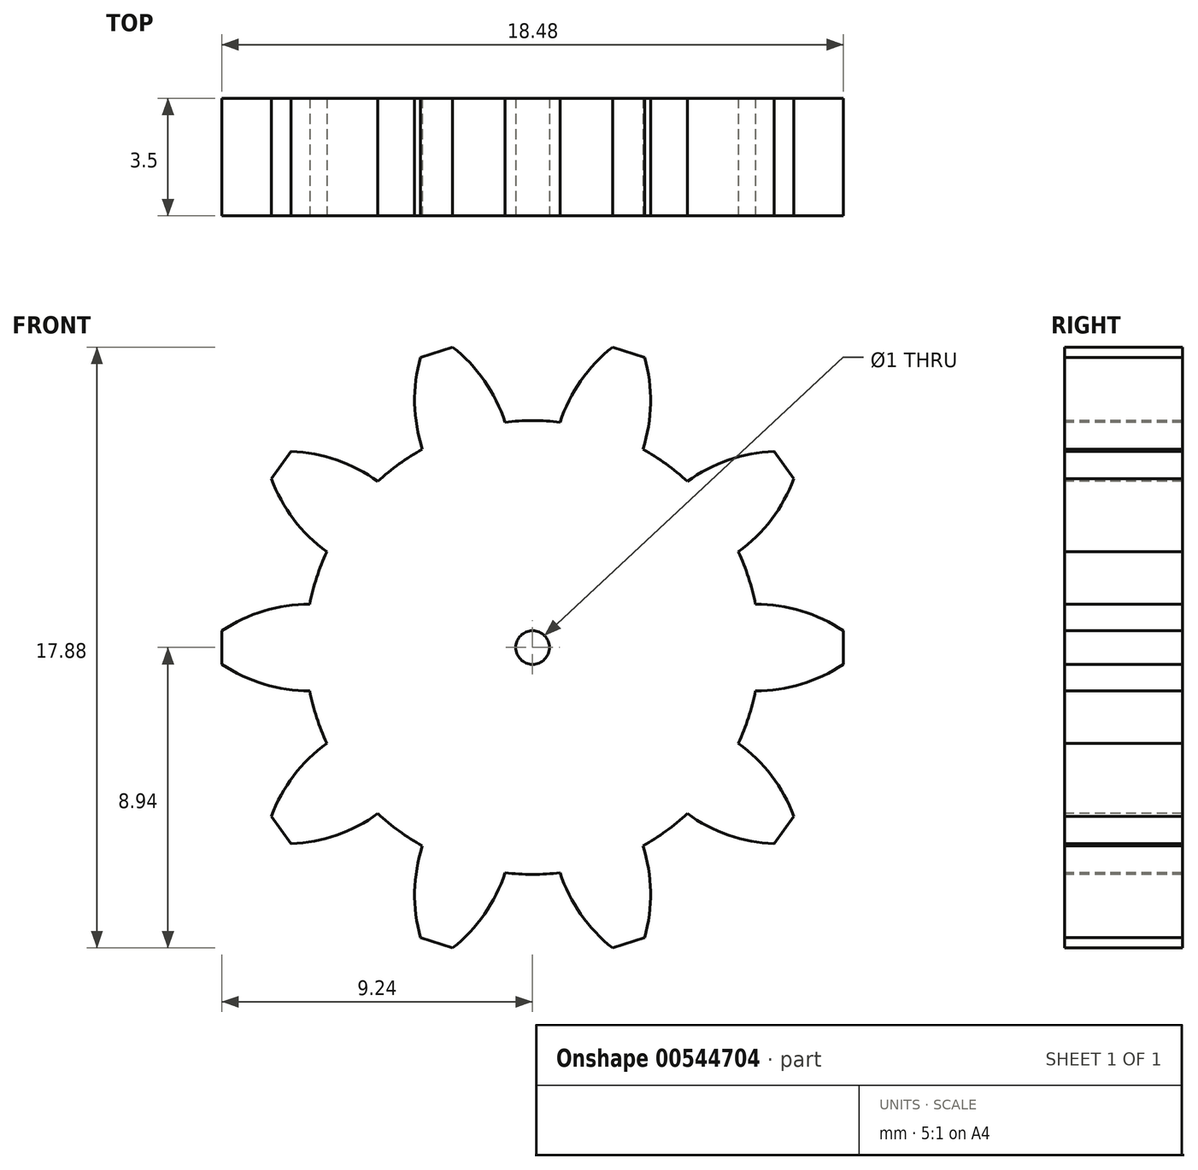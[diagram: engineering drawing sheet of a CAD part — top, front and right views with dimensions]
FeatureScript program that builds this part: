
annotation { "Feature Type Name" : "Feature", "Feature Type Description" : "" }
export const myFeature = defineFeature(function(context is Context, id is Id, definition is map)
    precondition{}
    {
        {
            var Q0;
            Q0=qCreatedBy(makeId("Front.planeOp"),FACE);
            var sketch = newSketch(context, id + "F0", { "sketchPlane" : qUnion([Q0])});
            skCircle(sketch, "E0", {"center": v(0, 0) * mm, "radius": 20 * mm, "construction": true});
            skCircle(sketch, "E1", {"center": v(0, 0) * mm, "radius": 24 * mm, "construction": true});
            skCircle(sketch, "E2", {"center": v(0, 0) * mm, "radius": 22.5 * mm, "construction": true});
            skPoint(sketch, "E3", {"position": v(0, 20) * mm});
            skPoint(sketch, "E4", {"position": v(-0.5, 20) * mm});
            skPoint(sketch, "E5", {"position": v(0.5, 20) * mm});
            skPoint(sketch, "E6", {"position": v(0, 22.5) * mm});
            skPoint(sketch, "E7", {"position": v(-1.3, 22.46) * mm});
            skPoint(sketch, "E8", {"position": v(1.3, 22.46) * mm});
            skArc(sketch, "E9", {"start": v(-1.3, 22.46) * mm, "mid": v(-1.1, 21.17) * mm, "end": v(-0.5, 20) * mm, "construction": true});
            skArc(sketch, "E10", {"start": v(0.5, 20) * mm, "mid": v(1.1, 21.17) * mm, "end": v(1.3, 22.46) * mm, "construction": true});
            skLineSegment(sketch, "E11", {"start": v(-0.5, 20) * mm, "end": v(0.5, 20) * mm, "construction": true});
            skPoint(sketch, "E12.1.0", {"position": v(-5.27, 19.3) * mm});
            skArc(sketch, "E12.1.1", {"start": v(-4.3, 19.53) * mm, "mid": v(-4, 20.81) * mm, "end": v(-4.11, 22.12) * mm, "construction": true});
            skArc(sketch, "E12.1.2", {"start": v(-6.64, 21.5) * mm, "mid": v(-6.13, 20.29) * mm, "end": v(-5.27, 19.3) * mm, "construction": true});
            skPoint(sketch, "E12.1.3", {"position": v(-6.64, 21.5) * mm});
            skPoint(sketch, "E12.1.4", {"position": v(-5.38, 21.85) * mm});
            skPoint(sketch, "E12.1.5", {"position": v(-4.3, 19.53) * mm});
            skPoint(sketch, "E12.1.6", {"position": v(-4.11, 22.12) * mm});
            skPoint(sketch, "E12.1.7", {"position": v(-4.79, 19.42) * mm});
            skLineSegment(sketch, "E12.1.8", {"start": v(-5.27, 19.3) * mm, "end": v(-4.3, 19.53) * mm, "construction": true});
            skPoint(sketch, "E12.2.0", {"position": v(-9.73, 17.47) * mm});
            skArc(sketch, "E12.2.1", {"start": v(-8.85, 17.94) * mm, "mid": v(-8.87, 19.25) * mm, "end": v(-9.29, 20.5) * mm, "construction": true});
            skArc(sketch, "E12.2.2", {"start": v(-11.59, 19.29) * mm, "mid": v(-10.8, 18.23) * mm, "end": v(-9.73, 17.47) * mm, "construction": true});
            skPoint(sketch, "E12.2.3", {"position": v(-11.59, 19.29) * mm});
            skPoint(sketch, "E12.2.4", {"position": v(-10.46, 19.92) * mm});
            skPoint(sketch, "E12.2.5", {"position": v(-8.85, 17.94) * mm});
            skPoint(sketch, "E12.2.6", {"position": v(-9.29, 20.5) * mm});
            skPoint(sketch, "E12.2.7", {"position": v(-9.3, 17.7) * mm});
            skLineSegment(sketch, "E12.2.8", {"start": v(-9.73, 17.47) * mm, "end": v(-8.85, 17.94) * mm, "construction": true});
            skPoint(sketch, "E12.3.0", {"position": v(-13.63, 14.63) * mm});
            skArc(sketch, "E12.3.1", {"start": v(-12.88, 15.3) * mm, "mid": v(-13.22, 16.57) * mm, "end": v(-13.92, 17.67) * mm, "construction": true});
            skArc(sketch, "E12.3.2", {"start": v(-15.87, 15.95) * mm, "mid": v(-14.85, 15.12) * mm, "end": v(-13.63, 14.63) * mm, "construction": true});
            skPoint(sketch, "E12.3.3", {"position": v(-15.87, 15.95) * mm});
            skPoint(sketch, "E12.3.4", {"position": v(-14.92, 16.84) * mm});
            skPoint(sketch, "E12.3.5", {"position": v(-12.88, 15.3) * mm});
            skPoint(sketch, "E12.3.6", {"position": v(-13.92, 17.67) * mm});
            skPoint(sketch, "E12.3.7", {"position": v(-13.26, 14.97) * mm});
            skLineSegment(sketch, "E12.3.8", {"start": v(-13.63, 14.63) * mm, "end": v(-12.88, 15.3) * mm, "construction": true});
            skPoint(sketch, "E12.4.0", {"position": v(-16.74, 10.95) * mm});
            skArc(sketch, "E12.4.1", {"start": v(-16.17, 11.77) * mm, "mid": v(-16.8, 12.92) * mm, "end": v(-17.75, 13.83) * mm, "construction": true});
            skArc(sketch, "E12.4.2", {"start": v(-19.22, 11.7) * mm, "mid": v(-18.04, 11.12) * mm, "end": v(-16.74, 10.95) * mm, "construction": true});
            skPoint(sketch, "E12.4.3", {"position": v(-19.22, 11.7) * mm});
            skPoint(sketch, "E12.4.4", {"position": v(-18.52, 12.78) * mm});
            skPoint(sketch, "E12.4.5", {"position": v(-16.17, 11.77) * mm});
            skPoint(sketch, "E12.4.6", {"position": v(-17.75, 13.83) * mm});
            skPoint(sketch, "E12.4.7", {"position": v(-16.46, 11.36) * mm});
            skLineSegment(sketch, "E12.4.8", {"start": v(-16.74, 10.95) * mm, "end": v(-16.17, 11.77) * mm, "construction": true});
            skPoint(sketch, "E12.5.0", {"position": v(-18.87, 6.62) * mm});
            skArc(sketch, "E12.5.1", {"start": v(-18.52, 7.56) * mm, "mid": v(-19.4, 8.53) * mm, "end": v(-20.54, 9.18) * mm, "construction": true});
            skArc(sketch, "E12.5.2", {"start": v(-21.46, 6.75) * mm, "mid": v(-20.18, 6.48) * mm, "end": v(-18.87, 6.62) * mm, "construction": true});
            skPoint(sketch, "E12.5.3", {"position": v(-21.46, 6.75) * mm});
            skPoint(sketch, "E12.5.4", {"position": v(-21.04, 7.98) * mm});
            skPoint(sketch, "E12.5.5", {"position": v(-18.52, 7.56) * mm});
            skPoint(sketch, "E12.5.6", {"position": v(-20.54, 9.18) * mm});
            skPoint(sketch, "E12.5.7", {"position": v(-18.7, 7.1) * mm});
            skLineSegment(sketch, "E12.5.8", {"start": v(-18.87, 6.62) * mm, "end": v(-18.52, 7.56) * mm, "construction": true});
            skPoint(sketch, "E12.6.0", {"position": v(-19.9, 1.91) * mm});
            skArc(sketch, "E12.6.1", {"start": v(-19.79, 2.9) * mm, "mid": v(-20.88, 3.64) * mm, "end": v(-22.14, 4) * mm, "construction": true});
            skArc(sketch, "E12.6.2", {"start": v(-22.46, 1.42) * mm, "mid": v(-21.14, 1.46) * mm, "end": v(-19.9, 1.91) * mm, "construction": true});
            skPoint(sketch, "E12.6.3", {"position": v(-22.46, 1.42) * mm});
            skPoint(sketch, "E12.6.4", {"position": v(-22.34, 2.71) * mm});
            skPoint(sketch, "E12.6.5", {"position": v(-19.79, 2.9) * mm});
            skPoint(sketch, "E12.6.6", {"position": v(-22.14, 4) * mm});
            skPoint(sketch, "E12.6.7", {"position": v(-19.85, 2.41) * mm});
            skLineSegment(sketch, "E12.6.8", {"start": v(-19.9, 1.91) * mm, "end": v(-19.79, 2.9) * mm, "construction": true});
            skPoint(sketch, "E12.7.0", {"position": v(-19.79, -2.9) * mm});
            skArc(sketch, "E12.7.1", {"start": v(-19.9, -1.91) * mm, "mid": v(-21.14, -1.46) * mm, "end": v(-22.46, -1.42) * mm, "construction": true});
            skArc(sketch, "E12.7.2", {"start": v(-22.14, -4) * mm, "mid": v(-20.88, -3.64) * mm, "end": v(-19.79, -2.9) * mm, "construction": true});
            skPoint(sketch, "E12.7.3", {"position": v(-22.14, -4) * mm});
            skPoint(sketch, "E12.7.4", {"position": v(-22.34, -2.71) * mm});
            skPoint(sketch, "E12.7.5", {"position": v(-19.9, -1.91) * mm});
            skPoint(sketch, "E12.7.6", {"position": v(-22.46, -1.42) * mm});
            skPoint(sketch, "E12.7.7", {"position": v(-19.85, -2.41) * mm});
            skLineSegment(sketch, "E12.7.8", {"start": v(-19.79, -2.9) * mm, "end": v(-19.9, -1.91) * mm, "construction": true});
            skPoint(sketch, "E12.8.0", {"position": v(-18.52, -7.56) * mm});
            skArc(sketch, "E12.8.1", {"start": v(-18.87, -6.62) * mm, "mid": v(-20.18, -6.48) * mm, "end": v(-21.46, -6.75) * mm, "construction": true});
            skArc(sketch, "E12.8.2", {"start": v(-20.54, -9.18) * mm, "mid": v(-19.4, -8.53) * mm, "end": v(-18.52, -7.56) * mm, "construction": true});
            skPoint(sketch, "E12.8.3", {"position": v(-20.54, -9.18) * mm});
            skPoint(sketch, "E12.8.4", {"position": v(-21.04, -7.98) * mm});
            skPoint(sketch, "E12.8.5", {"position": v(-18.87, -6.62) * mm});
            skPoint(sketch, "E12.8.6", {"position": v(-21.46, -6.75) * mm});
            skPoint(sketch, "E12.8.7", {"position": v(-18.7, -7.1) * mm});
            skLineSegment(sketch, "E12.8.8", {"start": v(-18.52, -7.56) * mm, "end": v(-18.87, -6.62) * mm, "construction": true});
            skPoint(sketch, "E12.9.0", {"position": v(-16.17, -11.77) * mm});
            skArc(sketch, "E12.9.1", {"start": v(-16.74, -10.95) * mm, "mid": v(-18.04, -11.12) * mm, "end": v(-19.22, -11.7) * mm, "construction": true});
            skArc(sketch, "E12.9.2", {"start": v(-17.75, -13.83) * mm, "mid": v(-16.8, -12.92) * mm, "end": v(-16.17, -11.77) * mm, "construction": true});
            skPoint(sketch, "E12.9.3", {"position": v(-17.75, -13.83) * mm});
            skPoint(sketch, "E12.9.4", {"position": v(-18.52, -12.78) * mm});
            skPoint(sketch, "E12.9.5", {"position": v(-16.74, -10.95) * mm});
            skPoint(sketch, "E12.9.6", {"position": v(-19.22, -11.7) * mm});
            skPoint(sketch, "E12.9.7", {"position": v(-16.46, -11.36) * mm});
            skLineSegment(sketch, "E12.9.8", {"start": v(-16.17, -11.77) * mm, "end": v(-16.74, -10.95) * mm, "construction": true});
            skPoint(sketch, "E12.10.0", {"position": v(-12.88, -15.3) * mm});
            skArc(sketch, "E12.10.1", {"start": v(-13.63, -14.63) * mm, "mid": v(-14.85, -15.12) * mm, "end": v(-15.87, -15.95) * mm, "construction": true});
            skArc(sketch, "E12.10.2", {"start": v(-13.92, -17.67) * mm, "mid": v(-13.22, -16.57) * mm, "end": v(-12.88, -15.3) * mm, "construction": true});
            skPoint(sketch, "E12.10.3", {"position": v(-13.92, -17.67) * mm});
            skPoint(sketch, "E12.10.4", {"position": v(-14.92, -16.84) * mm});
            skPoint(sketch, "E12.10.5", {"position": v(-13.63, -14.63) * mm});
            skPoint(sketch, "E12.10.6", {"position": v(-15.87, -15.95) * mm});
            skPoint(sketch, "E12.10.7", {"position": v(-13.26, -14.97) * mm});
            skLineSegment(sketch, "E12.10.8", {"start": v(-12.88, -15.3) * mm, "end": v(-13.63, -14.63) * mm, "construction": true});
            skPoint(sketch, "E12.11.0", {"position": v(-8.85, -17.94) * mm});
            skArc(sketch, "E12.11.1", {"start": v(-9.73, -17.47) * mm, "mid": v(-10.8, -18.23) * mm, "end": v(-11.59, -19.29) * mm, "construction": true});
            skArc(sketch, "E12.11.2", {"start": v(-9.29, -20.5) * mm, "mid": v(-8.87, -19.25) * mm, "end": v(-8.85, -17.94) * mm, "construction": true});
            skPoint(sketch, "E12.11.3", {"position": v(-9.29, -20.5) * mm});
            skPoint(sketch, "E12.11.4", {"position": v(-10.46, -19.92) * mm});
            skPoint(sketch, "E12.11.5", {"position": v(-9.73, -17.47) * mm});
            skPoint(sketch, "E12.11.6", {"position": v(-11.59, -19.29) * mm});
            skPoint(sketch, "E12.11.7", {"position": v(-9.3, -17.7) * mm});
            skLineSegment(sketch, "E12.11.8", {"start": v(-8.85, -17.94) * mm, "end": v(-9.73, -17.47) * mm, "construction": true});
            skPoint(sketch, "E12.12.0", {"position": v(-4.3, -19.53) * mm});
            skArc(sketch, "E12.12.1", {"start": v(-5.27, -19.3) * mm, "mid": v(-6.13, -20.29) * mm, "end": v(-6.64, -21.5) * mm, "construction": true});
            skArc(sketch, "E12.12.2", {"start": v(-4.11, -22.12) * mm, "mid": v(-4, -20.81) * mm, "end": v(-4.3, -19.53) * mm, "construction": true});
            skPoint(sketch, "E12.12.3", {"position": v(-4.11, -22.12) * mm});
            skPoint(sketch, "E12.12.4", {"position": v(-5.38, -21.85) * mm});
            skPoint(sketch, "E12.12.5", {"position": v(-5.27, -19.3) * mm});
            skPoint(sketch, "E12.12.6", {"position": v(-6.64, -21.5) * mm});
            skPoint(sketch, "E12.12.7", {"position": v(-4.79, -19.42) * mm});
            skLineSegment(sketch, "E12.12.8", {"start": v(-4.3, -19.53) * mm, "end": v(-5.27, -19.3) * mm, "construction": true});
            skPoint(sketch, "E12.13.0", {"position": v(0.5, -20) * mm});
            skArc(sketch, "E12.13.1", {"start": v(-0.5, -20) * mm, "mid": v(-1.1, -21.17) * mm, "end": v(-1.3, -22.46) * mm, "construction": true});
            skArc(sketch, "E12.13.2", {"start": v(1.3, -22.46) * mm, "mid": v(1.1, -21.17) * mm, "end": v(0.5, -20) * mm, "construction": true});
            skPoint(sketch, "E12.13.3", {"position": v(1.3, -22.46) * mm});
            skPoint(sketch, "E12.13.4", {"position": v(0, -22.5) * mm});
            skPoint(sketch, "E12.13.5", {"position": v(-0.5, -20) * mm});
            skPoint(sketch, "E12.13.6", {"position": v(-1.3, -22.46) * mm});
            skPoint(sketch, "E12.13.7", {"position": v(0, -20) * mm});
            skLineSegment(sketch, "E12.13.8", {"start": v(0.5, -20) * mm, "end": v(-0.5, -20) * mm, "construction": true});
            skPoint(sketch, "E12.14.0", {"position": v(5.27, -19.3) * mm});
            skArc(sketch, "E12.14.1", {"start": v(4.3, -19.53) * mm, "mid": v(4, -20.81) * mm, "end": v(4.11, -22.12) * mm, "construction": true});
            skArc(sketch, "E12.14.2", {"start": v(6.64, -21.5) * mm, "mid": v(6.13, -20.29) * mm, "end": v(5.27, -19.3) * mm, "construction": true});
            skPoint(sketch, "E12.14.3", {"position": v(6.64, -21.5) * mm});
            skPoint(sketch, "E12.14.4", {"position": v(5.38, -21.85) * mm});
            skPoint(sketch, "E12.14.5", {"position": v(4.3, -19.53) * mm});
            skPoint(sketch, "E12.14.6", {"position": v(4.11, -22.12) * mm});
            skPoint(sketch, "E12.14.7", {"position": v(4.79, -19.42) * mm});
            skLineSegment(sketch, "E12.14.8", {"start": v(5.27, -19.3) * mm, "end": v(4.3, -19.53) * mm, "construction": true});
            skPoint(sketch, "E12.15.0", {"position": v(9.73, -17.47) * mm});
            skArc(sketch, "E12.15.1", {"start": v(8.85, -17.94) * mm, "mid": v(8.87, -19.25) * mm, "end": v(9.29, -20.5) * mm, "construction": true});
            skArc(sketch, "E12.15.2", {"start": v(11.59, -19.29) * mm, "mid": v(10.8, -18.23) * mm, "end": v(9.73, -17.47) * mm, "construction": true});
            skPoint(sketch, "E12.15.3", {"position": v(11.59, -19.29) * mm});
            skPoint(sketch, "E12.15.4", {"position": v(10.46, -19.92) * mm});
            skPoint(sketch, "E12.15.5", {"position": v(8.85, -17.94) * mm});
            skPoint(sketch, "E12.15.6", {"position": v(9.29, -20.5) * mm});
            skPoint(sketch, "E12.15.7", {"position": v(9.3, -17.7) * mm});
            skLineSegment(sketch, "E12.15.8", {"start": v(9.73, -17.47) * mm, "end": v(8.85, -17.94) * mm, "construction": true});
            skPoint(sketch, "E12.16.0", {"position": v(13.63, -14.63) * mm});
            skArc(sketch, "E12.16.1", {"start": v(12.88, -15.3) * mm, "mid": v(13.22, -16.57) * mm, "end": v(13.92, -17.67) * mm, "construction": true});
            skArc(sketch, "E12.16.2", {"start": v(15.87, -15.95) * mm, "mid": v(14.85, -15.12) * mm, "end": v(13.63, -14.63) * mm, "construction": true});
            skPoint(sketch, "E12.16.3", {"position": v(15.87, -15.95) * mm});
            skPoint(sketch, "E12.16.4", {"position": v(14.92, -16.84) * mm});
            skPoint(sketch, "E12.16.5", {"position": v(12.88, -15.3) * mm});
            skPoint(sketch, "E12.16.6", {"position": v(13.92, -17.67) * mm});
            skPoint(sketch, "E12.16.7", {"position": v(13.26, -14.97) * mm});
            skLineSegment(sketch, "E12.16.8", {"start": v(13.63, -14.63) * mm, "end": v(12.88, -15.3) * mm, "construction": true});
            skPoint(sketch, "E12.17.0", {"position": v(16.74, -10.95) * mm});
            skArc(sketch, "E12.17.1", {"start": v(16.17, -11.77) * mm, "mid": v(16.8, -12.92) * mm, "end": v(17.75, -13.83) * mm, "construction": true});
            skArc(sketch, "E12.17.2", {"start": v(19.22, -11.7) * mm, "mid": v(18.04, -11.12) * mm, "end": v(16.74, -10.95) * mm, "construction": true});
            skPoint(sketch, "E12.17.3", {"position": v(19.22, -11.7) * mm});
            skPoint(sketch, "E12.17.4", {"position": v(18.52, -12.78) * mm});
            skPoint(sketch, "E12.17.5", {"position": v(16.17, -11.77) * mm});
            skPoint(sketch, "E12.17.6", {"position": v(17.75, -13.83) * mm});
            skPoint(sketch, "E12.17.7", {"position": v(16.46, -11.36) * mm});
            skLineSegment(sketch, "E12.17.8", {"start": v(16.74, -10.95) * mm, "end": v(16.17, -11.77) * mm, "construction": true});
            skPoint(sketch, "E12.18.0", {"position": v(18.87, -6.62) * mm});
            skArc(sketch, "E12.18.1", {"start": v(18.52, -7.56) * mm, "mid": v(19.4, -8.53) * mm, "end": v(20.54, -9.18) * mm, "construction": true});
            skArc(sketch, "E12.18.2", {"start": v(21.46, -6.75) * mm, "mid": v(20.18, -6.48) * mm, "end": v(18.87, -6.62) * mm, "construction": true});
            skPoint(sketch, "E12.18.3", {"position": v(21.46, -6.75) * mm});
            skPoint(sketch, "E12.18.4", {"position": v(21.04, -7.98) * mm});
            skPoint(sketch, "E12.18.5", {"position": v(18.52, -7.56) * mm});
            skPoint(sketch, "E12.18.6", {"position": v(20.54, -9.18) * mm});
            skPoint(sketch, "E12.18.7", {"position": v(18.7, -7.1) * mm});
            skLineSegment(sketch, "E12.18.8", {"start": v(18.87, -6.62) * mm, "end": v(18.52, -7.56) * mm, "construction": true});
            skPoint(sketch, "E12.19.0", {"position": v(19.9, -1.91) * mm});
            skArc(sketch, "E12.19.1", {"start": v(19.79, -2.9) * mm, "mid": v(20.88, -3.64) * mm, "end": v(22.14, -4) * mm, "construction": true});
            skArc(sketch, "E12.19.2", {"start": v(22.46, -1.42) * mm, "mid": v(21.14, -1.46) * mm, "end": v(19.9, -1.91) * mm, "construction": true});
            skPoint(sketch, "E12.19.3", {"position": v(22.46, -1.42) * mm});
            skPoint(sketch, "E12.19.4", {"position": v(22.34, -2.71) * mm});
            skPoint(sketch, "E12.19.5", {"position": v(19.79, -2.9) * mm});
            skPoint(sketch, "E12.19.6", {"position": v(22.14, -4) * mm});
            skPoint(sketch, "E12.19.7", {"position": v(19.85, -2.41) * mm});
            skLineSegment(sketch, "E12.19.8", {"start": v(19.9, -1.91) * mm, "end": v(19.79, -2.9) * mm, "construction": true});
            skPoint(sketch, "E12.20.0", {"position": v(19.79, 2.9) * mm});
            skArc(sketch, "E12.20.1", {"start": v(19.9, 1.91) * mm, "mid": v(21.14, 1.46) * mm, "end": v(22.46, 1.42) * mm, "construction": true});
            skArc(sketch, "E12.20.2", {"start": v(22.14, 4) * mm, "mid": v(20.88, 3.64) * mm, "end": v(19.79, 2.9) * mm, "construction": true});
            skPoint(sketch, "E12.20.3", {"position": v(22.14, 4) * mm});
            skPoint(sketch, "E12.20.4", {"position": v(22.34, 2.71) * mm});
            skPoint(sketch, "E12.20.5", {"position": v(19.9, 1.91) * mm});
            skPoint(sketch, "E12.20.6", {"position": v(22.46, 1.42) * mm});
            skPoint(sketch, "E12.20.7", {"position": v(19.85, 2.41) * mm});
            skLineSegment(sketch, "E12.20.8", {"start": v(19.79, 2.9) * mm, "end": v(19.9, 1.91) * mm, "construction": true});
            skPoint(sketch, "E12.21.0", {"position": v(18.52, 7.56) * mm});
            skArc(sketch, "E12.21.1", {"start": v(18.87, 6.62) * mm, "mid": v(20.18, 6.48) * mm, "end": v(21.46, 6.75) * mm, "construction": true});
            skArc(sketch, "E12.21.2", {"start": v(20.54, 9.18) * mm, "mid": v(19.4, 8.53) * mm, "end": v(18.52, 7.56) * mm, "construction": true});
            skPoint(sketch, "E12.21.3", {"position": v(20.54, 9.18) * mm});
            skPoint(sketch, "E12.21.4", {"position": v(21.04, 7.98) * mm});
            skPoint(sketch, "E12.21.5", {"position": v(18.87, 6.62) * mm});
            skPoint(sketch, "E12.21.6", {"position": v(21.46, 6.75) * mm});
            skPoint(sketch, "E12.21.7", {"position": v(18.7, 7.1) * mm});
            skLineSegment(sketch, "E12.21.8", {"start": v(18.52, 7.56) * mm, "end": v(18.87, 6.62) * mm, "construction": true});
            skPoint(sketch, "E12.22.0", {"position": v(16.17, 11.77) * mm});
            skArc(sketch, "E12.22.1", {"start": v(16.74, 10.95) * mm, "mid": v(18.04, 11.12) * mm, "end": v(19.22, 11.7) * mm, "construction": true});
            skArc(sketch, "E12.22.2", {"start": v(17.75, 13.83) * mm, "mid": v(16.8, 12.92) * mm, "end": v(16.17, 11.77) * mm, "construction": true});
            skPoint(sketch, "E12.22.3", {"position": v(17.75, 13.83) * mm});
            skPoint(sketch, "E12.22.4", {"position": v(18.52, 12.78) * mm});
            skPoint(sketch, "E12.22.5", {"position": v(16.74, 10.95) * mm});
            skPoint(sketch, "E12.22.6", {"position": v(19.22, 11.7) * mm});
            skPoint(sketch, "E12.22.7", {"position": v(16.46, 11.36) * mm});
            skLineSegment(sketch, "E12.22.8", {"start": v(16.17, 11.77) * mm, "end": v(16.74, 10.95) * mm, "construction": true});
            skPoint(sketch, "E12.23.0", {"position": v(12.88, 15.3) * mm});
            skArc(sketch, "E12.23.1", {"start": v(13.63, 14.63) * mm, "mid": v(14.85, 15.12) * mm, "end": v(15.87, 15.95) * mm, "construction": true});
            skArc(sketch, "E12.23.2", {"start": v(13.92, 17.67) * mm, "mid": v(13.22, 16.57) * mm, "end": v(12.88, 15.3) * mm, "construction": true});
            skPoint(sketch, "E12.23.3", {"position": v(13.92, 17.67) * mm});
            skPoint(sketch, "E12.23.4", {"position": v(14.92, 16.84) * mm});
            skPoint(sketch, "E12.23.5", {"position": v(13.63, 14.63) * mm});
            skPoint(sketch, "E12.23.6", {"position": v(15.87, 15.95) * mm});
            skPoint(sketch, "E12.23.7", {"position": v(13.26, 14.97) * mm});
            skLineSegment(sketch, "E12.23.8", {"start": v(12.88, 15.3) * mm, "end": v(13.63, 14.63) * mm, "construction": true});
            skPoint(sketch, "E12.24.0", {"position": v(8.85, 17.94) * mm});
            skArc(sketch, "E12.24.1", {"start": v(9.73, 17.47) * mm, "mid": v(10.8, 18.23) * mm, "end": v(11.59, 19.29) * mm, "construction": true});
            skArc(sketch, "E12.24.2", {"start": v(9.29, 20.5) * mm, "mid": v(8.87, 19.25) * mm, "end": v(8.85, 17.94) * mm, "construction": true});
            skPoint(sketch, "E12.24.3", {"position": v(9.29, 20.5) * mm});
            skPoint(sketch, "E12.24.4", {"position": v(10.46, 19.92) * mm});
            skPoint(sketch, "E12.24.5", {"position": v(9.73, 17.47) * mm});
            skPoint(sketch, "E12.24.6", {"position": v(11.59, 19.29) * mm});
            skPoint(sketch, "E12.24.7", {"position": v(9.3, 17.7) * mm});
            skLineSegment(sketch, "E12.24.8", {"start": v(8.85, 17.94) * mm, "end": v(9.73, 17.47) * mm, "construction": true});
            skPoint(sketch, "E13.0.25.0", {"position": v(4.3, 19.53) * mm});
            skArc(sketch, "E13.1.25.0", {"start": v(5.27, 19.3) * mm, "mid": v(6.13, 20.29) * mm, "end": v(6.64, 21.5) * mm, "construction": true});
            skArc(sketch, "E13.5.25.0", {"start": v(4.11, 22.12) * mm, "mid": v(4, 20.81) * mm, "end": v(4.3, 19.53) * mm, "construction": true});
            skPoint(sketch, "E13.9.25.0", {"position": v(4.11, 22.12) * mm});
            skPoint(sketch, "E13.10.25.0", {"position": v(5.38, 21.85) * mm});
            skPoint(sketch, "E13.11.25.0", {"position": v(5.27, 19.3) * mm});
            skPoint(sketch, "E13.12.25.0", {"position": v(6.64, 21.5) * mm});
            skPoint(sketch, "E13.13.25.0", {"position": v(4.79, 19.42) * mm});
            skLineSegment(sketch, "E13.14.25.0", {"start": v(4.3, 19.53) * mm, "end": v(5.27, 19.3) * mm, "construction": true});
            skArc(sketch, "E14", {"start": v(-22.46, -1.42) * mm, "mid": v(-22.5, 0) * mm, "end": v(-22.46, 1.42) * mm});
            skPoint(sketch, "E15", {"position": v(-22.5, 0) * mm});
            skLineSegment(sketch, "E16", {"start": v(-22.5, 0) * mm, "end": v(0, 0) * mm, "construction": true});
            skCircle(sketch, "E17", {"center": v(0, 0) * mm, "radius": 4 * mm, "construction": true});
            skCircle(sketch, "E18", {"center": v(0, 0) * mm, "radius": 1.5 * mm, "construction": true});
            skPoint(sketch, "E19", {"position": v(-20, 0) * mm});
            skLineSegment(sketch, "E20", {"start": v(-20, 0) * mm, "end": v(-22.5, 0) * mm});
            skLineSegment(sketch, "E21", {"start": v(-1.5, 0) * mm, "end": v(-4, 0) * mm});
            skPoint(sketch, "E22", {"position": v(-2.75, 0) * mm});
            skPoint(sketch, "E23", {"position": v(-21.25, 0) * mm});
            skCircle(sketch, "E24", {"center": v(-12, 0) * mm, "radius": 9.25 * mm, "construction": true});
            skCircle(sketch, "E25", {"center": v(-12, 0) * mm, "radius": 6.75 * mm});
            skPoint(sketch, "E26", {"position": v(-18.75, 0) * mm});
            skPoint(sketch, "E27", {"position": v(-18.63, 1.3) * mm});
            skPoint(sketch, "E28", {"position": v(-18.63, -1.3) * mm});
            skPoint(sketch, "E29", {"position": v(-21.24, 0.5) * mm});
            skPoint(sketch, "E30", {"position": v(-21.24, -0.5) * mm});
            skLineSegment(sketch, "E31", {"start": v(-21.24, 0.5) * mm, "end": v(-21.24, -0.5) * mm});
            skArc(sketch, "E32", {"start": v(-18.63, 1.3) * mm, "mid": v(-19.99, 1.1) * mm, "end": v(-21.24, 0.5) * mm});
            skArc(sketch, "E33", {"start": v(-21.24, -0.5) * mm, "mid": v(-19.99, -1.1) * mm, "end": v(-18.63, -1.3) * mm});
            skCircle(sketch, "E34", {"center": v(-12, 0) * mm, "radius": 0.5 * mm});
            skPoint(sketch, "E35.1.0", {"position": v(-19.77, -5.02) * mm});
            skPoint(sketch, "E35.1.1", {"position": v(-19.18, -5.83) * mm});
            skArc(sketch, "E35.1.2", {"start": v(-19.18, -5.83) * mm, "mid": v(-17.82, -5.58) * mm, "end": v(-16.6, -4.94) * mm});
            skPoint(sketch, "E35.1.3", {"position": v(-19.48, -5.44) * mm});
            skPoint(sketch, "E35.1.4", {"position": v(-17.46, -3.97) * mm});
            skPoint(sketch, "E35.1.5", {"position": v(-16.6, -4.94) * mm});
            skLineSegment(sketch, "E35.1.6", {"start": v(-19.77, -5.02) * mm, "end": v(-19.18, -5.83) * mm});
            skPoint(sketch, "E35.1.7", {"position": v(-18.47, -4.7) * mm});
            skArc(sketch, "E35.1.8", {"start": v(-18.12, -2.85) * mm, "mid": v(-19.1, -3.81) * mm, "end": v(-19.77, -5.02) * mm});
            skPoint(sketch, "E35.2.0", {"position": v(-15.33, -8.63) * mm});
            skPoint(sketch, "E35.2.1", {"position": v(-14.38, -8.94) * mm});
            skArc(sketch, "E35.2.2", {"start": v(-14.38, -8.94) * mm, "mid": v(-13.43, -7.94) * mm, "end": v(-12.82, -6.7) * mm});
            skPoint(sketch, "E35.2.3", {"position": v(-14.86, -8.8) * mm});
            skPoint(sketch, "E35.2.4", {"position": v(-14.09, -6.42) * mm});
            skPoint(sketch, "E35.2.5", {"position": v(-12.82, -6.7) * mm});
            skLineSegment(sketch, "E35.2.6", {"start": v(-15.33, -8.63) * mm, "end": v(-14.38, -8.94) * mm});
            skPoint(sketch, "E35.2.7", {"position": v(-14.47, -7.6) * mm});
            skArc(sketch, "E35.2.8", {"start": v(-15.28, -5.9) * mm, "mid": v(-15.5, -7.26) * mm, "end": v(-15.33, -8.63) * mm});
            skPoint(sketch, "E35.3.0", {"position": v(-9.62, -8.94) * mm});
            skPoint(sketch, "E35.3.1", {"position": v(-8.67, -8.63) * mm});
            skArc(sketch, "E35.3.2", {"start": v(-8.67, -8.63) * mm, "mid": v(-8.5, -7.26) * mm, "end": v(-8.72, -5.9) * mm});
            skPoint(sketch, "E35.3.3", {"position": v(-9.14, -8.8) * mm});
            skPoint(sketch, "E35.3.4", {"position": v(-9.91, -6.42) * mm});
            skPoint(sketch, "E35.3.5", {"position": v(-8.72, -5.9) * mm});
            skLineSegment(sketch, "E35.3.6", {"start": v(-9.62, -8.94) * mm, "end": v(-8.67, -8.63) * mm});
            skPoint(sketch, "E35.3.7", {"position": v(-9.53, -7.6) * mm});
            skArc(sketch, "E35.3.8", {"start": v(-11.18, -6.7) * mm, "mid": v(-10.57, -7.94) * mm, "end": v(-9.62, -8.94) * mm});
            skPoint(sketch, "E35.4.0", {"position": v(-4.82, -5.83) * mm});
            skPoint(sketch, "E35.4.1", {"position": v(-4.23, -5.02) * mm});
            skArc(sketch, "E35.4.2", {"start": v(-4.23, -5.02) * mm, "mid": v(-4.9, -3.81) * mm, "end": v(-5.88, -2.85) * mm});
            skPoint(sketch, "E35.4.3", {"position": v(-4.52, -5.44) * mm});
            skPoint(sketch, "E35.4.4", {"position": v(-6.54, -3.97) * mm});
            skPoint(sketch, "E35.4.5", {"position": v(-5.88, -2.85) * mm});
            skLineSegment(sketch, "E35.4.6", {"start": v(-4.82, -5.83) * mm, "end": v(-4.23, -5.02) * mm});
            skPoint(sketch, "E35.4.7", {"position": v(-5.53, -4.7) * mm});
            skArc(sketch, "E35.4.8", {"start": v(-7.4, -4.94) * mm, "mid": v(-6.18, -5.58) * mm, "end": v(-4.82, -5.83) * mm});
            skPoint(sketch, "E35.5.0", {"position": v(-2.76, -0.5) * mm});
            skPoint(sketch, "E35.5.1", {"position": v(-2.76, 0.5) * mm});
            skArc(sketch, "E35.5.2", {"start": v(-2.76, 0.5) * mm, "mid": v(-4.01, 1.1) * mm, "end": v(-5.37, 1.3) * mm});
            skPoint(sketch, "E35.5.4", {"position": v(-5.25, 0) * mm});
            skPoint(sketch, "E35.5.5", {"position": v(-5.37, 1.3) * mm});
            skLineSegment(sketch, "E35.5.6", {"start": v(-2.76, -0.5) * mm, "end": v(-2.76, 0.5) * mm});
            skPoint(sketch, "E35.5.7", {"position": v(-4, 0) * mm});
            skArc(sketch, "E35.5.8", {"start": v(-5.37, -1.3) * mm, "mid": v(-4.01, -1.1) * mm, "end": v(-2.76, -0.5) * mm});
            skPoint(sketch, "E35.6.0", {"position": v(-4.23, 5.02) * mm});
            skPoint(sketch, "E35.6.1", {"position": v(-4.82, 5.83) * mm});
            skArc(sketch, "E35.6.2", {"start": v(-4.82, 5.83) * mm, "mid": v(-6.18, 5.58) * mm, "end": v(-7.4, 4.94) * mm});
            skPoint(sketch, "E35.6.3", {"position": v(-4.52, 5.44) * mm});
            skPoint(sketch, "E35.6.4", {"position": v(-6.54, 3.97) * mm});
            skPoint(sketch, "E35.6.5", {"position": v(-7.4, 4.94) * mm});
            skLineSegment(sketch, "E35.6.6", {"start": v(-4.23, 5.02) * mm, "end": v(-4.82, 5.83) * mm});
            skPoint(sketch, "E35.6.7", {"position": v(-5.53, 4.7) * mm});
            skArc(sketch, "E35.6.8", {"start": v(-5.88, 2.85) * mm, "mid": v(-4.9, 3.81) * mm, "end": v(-4.23, 5.02) * mm});
            skPoint(sketch, "E35.7.0", {"position": v(-8.67, 8.63) * mm});
            skPoint(sketch, "E35.7.1", {"position": v(-9.62, 8.94) * mm});
            skArc(sketch, "E35.7.2", {"start": v(-9.62, 8.94) * mm, "mid": v(-10.57, 7.94) * mm, "end": v(-11.18, 6.7) * mm});
            skPoint(sketch, "E35.7.3", {"position": v(-9.14, 8.8) * mm});
            skPoint(sketch, "E35.7.4", {"position": v(-9.91, 6.42) * mm});
            skPoint(sketch, "E35.7.5", {"position": v(-11.18, 6.7) * mm});
            skLineSegment(sketch, "E35.7.6", {"start": v(-8.67, 8.63) * mm, "end": v(-9.62, 8.94) * mm});
            skPoint(sketch, "E35.7.7", {"position": v(-9.53, 7.6) * mm});
            skArc(sketch, "E35.7.8", {"start": v(-8.72, 5.9) * mm, "mid": v(-8.5, 7.26) * mm, "end": v(-8.67, 8.63) * mm});
            skPoint(sketch, "E35.8.0", {"position": v(-14.38, 8.94) * mm});
            skPoint(sketch, "E35.8.1", {"position": v(-15.33, 8.63) * mm});
            skArc(sketch, "E35.8.2", {"start": v(-15.33, 8.63) * mm, "mid": v(-15.5, 7.26) * mm, "end": v(-15.28, 5.9) * mm});
            skPoint(sketch, "E35.8.3", {"position": v(-14.86, 8.8) * mm});
            skPoint(sketch, "E35.8.4", {"position": v(-14.09, 6.42) * mm});
            skPoint(sketch, "E35.8.5", {"position": v(-15.28, 5.9) * mm});
            skLineSegment(sketch, "E35.8.6", {"start": v(-14.38, 8.94) * mm, "end": v(-15.33, 8.63) * mm});
            skPoint(sketch, "E35.8.7", {"position": v(-14.47, 7.6) * mm});
            skArc(sketch, "E35.8.8", {"start": v(-12.82, 6.7) * mm, "mid": v(-13.43, 7.94) * mm, "end": v(-14.38, 8.94) * mm});
            skPoint(sketch, "E36.0.9.0", {"position": v(-19.77, 5.02) * mm});
            skPoint(sketch, "E36.1.9.0", {"position": v(-19.18, 5.83) * mm});
            skArc(sketch, "E36.2.9.0", {"start": v(-19.77, 5.02) * mm, "mid": v(-19.1, 3.81) * mm, "end": v(-18.12, 2.85) * mm});
            skPoint(sketch, "E36.6.9.0", {"position": v(-19.48, 5.44) * mm});
            skPoint(sketch, "E36.7.9.0", {"position": v(-17.46, 3.97) * mm});
            skPoint(sketch, "E36.8.9.0", {"position": v(-18.12, 2.85) * mm});
            skLineSegment(sketch, "E36.9.9.0", {"start": v(-19.18, 5.83) * mm, "end": v(-19.77, 5.02) * mm});
            skPoint(sketch, "E36.12.9.0", {"position": v(-18.47, 4.7) * mm});
            skArc(sketch, "E36.13.9.0", {"start": v(-16.6, 4.94) * mm, "mid": v(-17.82, 5.58) * mm, "end": v(-19.18, 5.83) * mm});
            skSolve(sketch);
        }
        {
            var Q0;
            Q0 = qSketchRegion(id + "F0", true);
            extrude(context, id + "F1", {"entities" : qUnion([Q0]), "oppositeDirection" : true, "depth" : 3.5 * mm, "offsetDistance" : 25 * mm});
        }
    });
